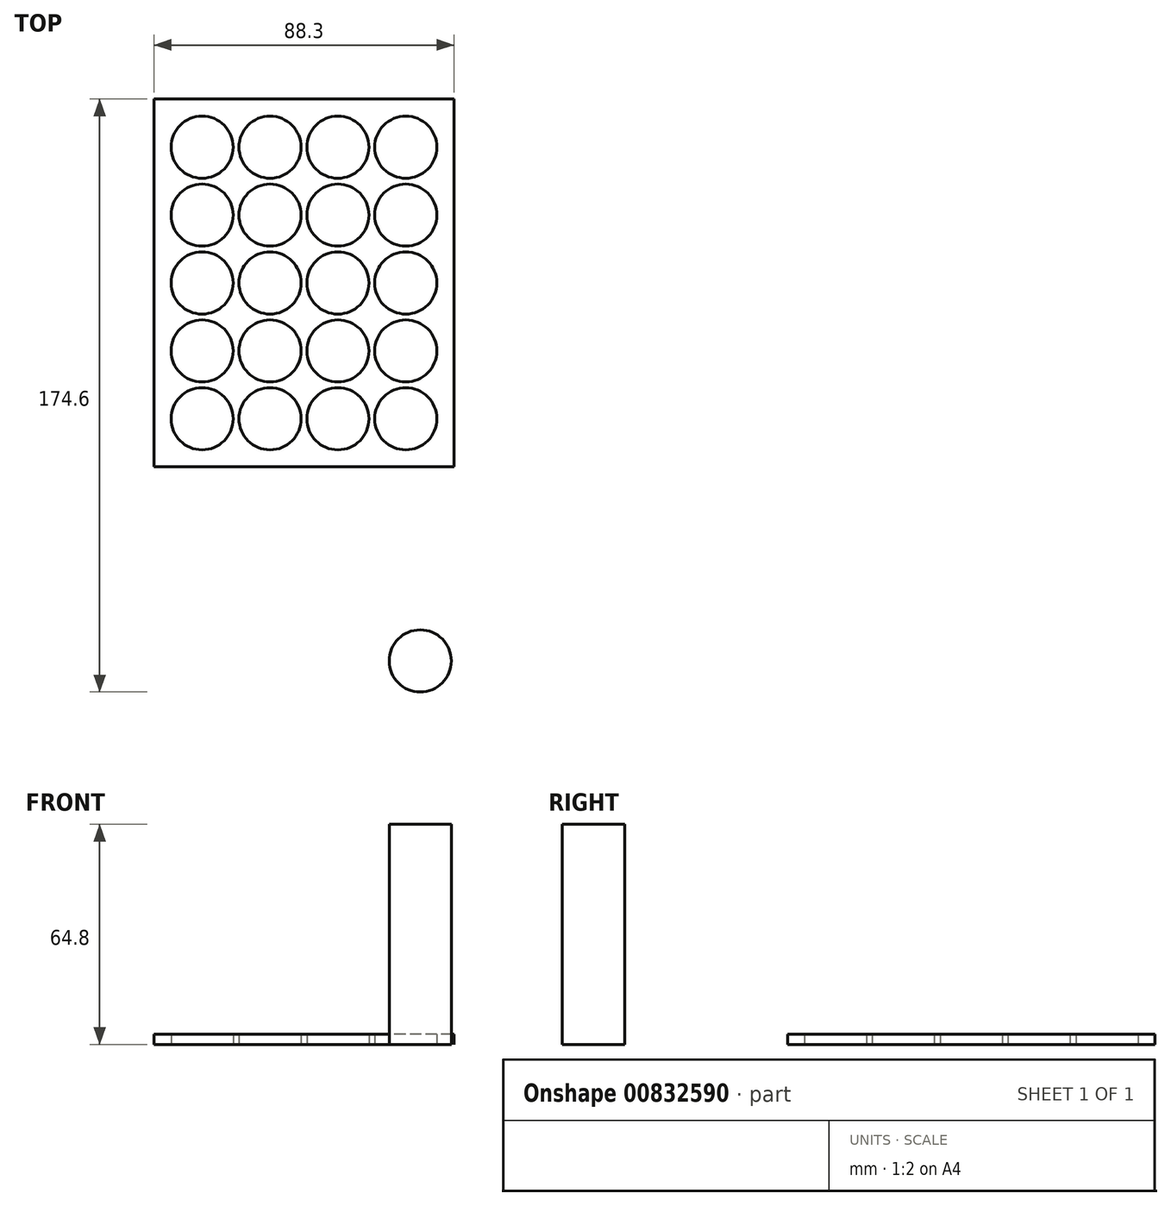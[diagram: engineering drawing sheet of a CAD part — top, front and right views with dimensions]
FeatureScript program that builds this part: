
annotation { "Feature Type Name" : "Feature", "Feature Type Description" : "" }
export const myFeature = defineFeature(function(context is Context, id is Id, definition is map)
    precondition{}
    {
        {
            var Q0;
            Q0=qCreatedBy(makeId("Top.planeOp"),FACE);
            var sketch = newSketch(context, id + "F0", { "sketchPlane" : qUnion([Q0])});
            skCircle(sketch, "E0", {"center": v(0, 0) * mm, "radius": 9.15 * mm});
            skSolve(sketch);
        }
        {
            var Q0;
            Q0=makeQuery(id+"F0.imprint","IMPRINT",FACE,{"disambiguationData":[TD([[makeQuery(id+"F0.imprint","IMPRINT",EDGE,{"derivedFrom":sQuery(id+"F0.wireOp",EDGE,"E0")}),1.0]])]});
            extrude(context, id + "F1", {"entities" : qUnion([Q0]), "depth" : 64.8 * mm, "offsetDistance" : 25 * mm});
        }
        {
            var Q0;
            Q0=qCreatedBy(makeId("Top.planeOp"),FACE);
            var sketch = newSketch(context, id + "F2", { "sketchPlane" : qUnion([Q0])});
            skCircle(sketch, "E1", {"center": v(-64.27, 71.3) * mm, "radius": 9.15 * mm});
            skLineSegment(sketch, "E2", {"start": v(-64.27, 71.3) * mm, "end": v(-84.27, 71.3) * mm});
            skCircle(sketch, "E3.0.1.0", {"center": v(-64.27, 91.3) * mm, "radius": 9.15 * mm});
            skCircle(sketch, "E3.0.2.0", {"center": v(-64.27, 111.3) * mm, "radius": 9.15 * mm});
            skCircle(sketch, "E3.0.3.0", {"center": v(-64.27, 131.3) * mm, "radius": 9.15 * mm});
            skCircle(sketch, "E3.0.4.0", {"center": v(-64.27, 151.3) * mm, "radius": 9.15 * mm});
            skCircle(sketch, "E3.1.0.0", {"center": v(-44.27, 71.3) * mm, "radius": 9.15 * mm});
            skCircle(sketch, "E3.1.1.0", {"center": v(-44.27, 91.3) * mm, "radius": 9.15 * mm});
            skCircle(sketch, "E3.1.2.0", {"center": v(-44.27, 111.3) * mm, "radius": 9.15 * mm});
            skCircle(sketch, "E3.1.3.0", {"center": v(-44.27, 131.3) * mm, "radius": 9.15 * mm});
            skCircle(sketch, "E3.1.4.0", {"center": v(-44.27, 151.3) * mm, "radius": 9.15 * mm});
            skCircle(sketch, "E3.2.0.0", {"center": v(-24.27, 71.3) * mm, "radius": 9.15 * mm});
            skCircle(sketch, "E3.2.1.0", {"center": v(-24.27, 91.3) * mm, "radius": 9.15 * mm});
            skCircle(sketch, "E3.2.2.0", {"center": v(-24.27, 111.3) * mm, "radius": 9.15 * mm});
            skCircle(sketch, "E3.2.3.0", {"center": v(-24.27, 131.3) * mm, "radius": 9.15 * mm});
            skCircle(sketch, "E3.2.4.0", {"center": v(-24.27, 151.3) * mm, "radius": 9.15 * mm});
            skCircle(sketch, "E3.3.0.0", {"center": v(-4.27, 71.3) * mm, "radius": 9.15 * mm});
            skCircle(sketch, "E3.3.1.0", {"center": v(-4.27, 91.3) * mm, "radius": 9.15 * mm});
            skCircle(sketch, "E3.3.2.0", {"center": v(-4.27, 111.3) * mm, "radius": 9.15 * mm});
            skCircle(sketch, "E3.3.3.0", {"center": v(-4.27, 131.3) * mm, "radius": 9.15 * mm});
            skCircle(sketch, "E3.3.4.0", {"center": v(-4.27, 151.3) * mm, "radius": 9.15 * mm});
            skLineSegment(sketch, "E3.direction1", {"start": v(-64.27, 71.3) * mm, "end": v(-44.27, 71.3) * mm, "construction": true});
            skLineSegment(sketch, "E3.direction2", {"start": v(-64.27, 71.3) * mm, "end": v(-64.27, 91.3) * mm, "construction": true});
            skLineSegment(sketch, "E4", {"start": v(9.88, 57.15) * mm, "end": v(9.88, 165.45) * mm});
            skLineSegment(sketch, "E5", {"start": v(9.88, 165.45) * mm, "end": v(-78.42, 165.45) * mm});
            skLineSegment(sketch, "E6", {"start": v(-78.42, 165.45) * mm, "end": v(-78.42, 57.15) * mm});
            skLineSegment(sketch, "E7", {"start": v(9.88, 57.15) * mm, "end": v(-78.42, 57.15) * mm});
            skSolve(sketch);
        }
        {
            var Q0;
            Q0=makeQuery(id+"F2.imprint","IMPRINT",FACE,{"disambiguationData":[TD([[makeQuery(id+"F2.imprint","IMPRINT",EDGE,{"derivedFrom":sQuery(id+"F2.wireOp",EDGE,"E1")}),-1.0]])]});
            extrude(context, id + "F3", {"entities" : qUnion([Q0]), "depth" : 3 * mm, "offsetDistance" : 25 * mm});
        }
    });
